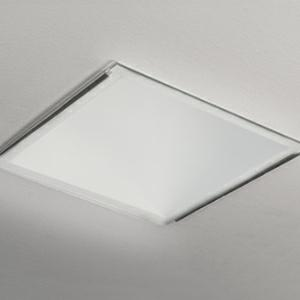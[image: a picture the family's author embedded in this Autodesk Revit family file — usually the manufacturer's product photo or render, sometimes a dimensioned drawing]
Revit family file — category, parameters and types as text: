
# Revit family: 3f_filippi_-_lucequadro_vs_3f_filippi_-_36575_-_lucequadro_led_2000_vs
name_source: partatom
category: Lighting Fixtures
units: mm (PartAtom-declared; Revit-internal decimal feet)

## family parameters
Cut with Voids When Loaded = No
Host = Face
Light Source = No
Part Type = Normal
Room Calculation Point = No
Round Connector Dimension = Use Diameter
Shared = No

## types (1)
- 3F Filippi - Lucequadro VS (1 x LED, 2291 lm, 20 W, 4000 K)
    Apparent Load = 20 VA
    Approval mark = ENEC
    CIE Flux Codes = 79 96 99 100 100
    Color Rendering = 80
    Color Temperature = 4000 K
    Control Gear = Electronic ballast
    Default Elevation = 1800 mm
    Description = ILLUMINOTECHNICAL
Luminous efficiency 100% (DLOR 100%, ULOR 0%).
Initial luminous flux of the luminaire 2291 lm.
Direct symmetric distribution.
Installation Interdistance Transv.D = 0.83 x hu - Long.D = 0.80 x hu.
Average luminance <3000 cd/m² for radial angles >65°.
Tabular UGR (CIE 117 - 4H-8H; S=0.25H; 70/50/20): RUG 17.2 - 17.
Beam angle: 58° - 57°.
Luminous efficacy 115 lm/W.
Lifetime (L90/B10): 30000 h. (tq+25°C)
Lifetime (L85/B10): 50000 h. (tq+25°C)
Lifetime (L70/B10): 80000 h. (tq+25°C)
Sudden decreased luminous flux after 50000 hours: 0% (C0).
Photobiological safety in compliance with IEC/TR 62778: RG1 low risk, (IEC 62471).
In compliance with IEC/EN 62722-2-1 - IEC/EN 62717 standards.

SOURCE
Compact LED module 2000/840.
Energy efficiency class (UE 2019/2020 - UE 2019/2015): D.
CIE 13.3 Colour rendering index: CRI >80 (R9 <50%).
IES TM-30 Fidelity Index: Rf = 84 Rg = 95.
CCT nominal colour temperature 4000 K.
Colour initial tolerance (MacAdam): SDCM 3.
Zhaga Book 3 compliant.

MECHANICAL
Housing in white painted steel.
Passive heat dissipator in anodised aluminium, oversized, for optimum thermal management of the LED module.
Flow recuperator in specular aluminium with superficial titanium-magnesium treatment, non-iridescent.
Moulded tempered anti-glare non-combustible glass, thickness 4 mm.
Lock-in mounting of the glass in the lateral seats in specular aluminium.
Fixing brackets in galvanised steel.
Slot-cover polycarbonate casings.
Dimensions: 235x235 mm, height 116 mm. Weight 2.11 kg.
IP44 protection degree for exposed part, IP20 for recessed part.
Mechanical strength to impacts IK08 (5 joule).
Glow-wire test resistance 960°C.

ELECTRICAL
Wiring on a separate unit.
Halogen Free electronic wiring 230V-50/60Hz, power factor 0.95, THD <25%, constant output current, SELV, class II, 1 driver.
Power of the luminaire 20 W.
CE - IEC 60598-1 - EN 60598-1.
SAFE FLICKER: PstLM=<1 and SVM=<0.4 (IEC TR 61547-1 and IEC TR 63158), to ensure a more comfortable and safe light.
Ambient temperature from 0°C to +25°C.
Temperature class T6 max 85°C.
Relative humidity UR: <85%.

INSTALLATION
Pull-up recessed fitting.
False ceiling carving: 210x210 mm.
All accessories dedicated to this product are available on the Catalog and on our website www.3F-Filippi.com.

ACCESSORIES
A0189 - Pair of reinforcing brackets for mineral fibre, metal and plasterboard panels, height 20 mm.

APPLICATIONS
Transit areas, corridors, commercial environments, display areas, shops and shop windows.

WARNING
Luminaire designed for disposal/recycling at end-of-life.
Replaceable (LED only) light source by a professional. Replaceable control gear by a professional.
    Height = 0 mm  [stored 0 ft]
    Lamp = 1 x LED
    Lamp Light Flux = 2291 lm
    Lamp Power = 20 W
    Lamp count = 1
    Length = 235 mm
    Lifetime = 50000 h
    Luminous efficacy = 115 lm/W
    Manufacturer = 3F Filippi
    ModVariant = No
    Model = 3F Filippi - 36575 - Lucequadro LED 2000 VS
    Mounting Place = Ceiling
    Mounting Type = Recessed
    Number of Poles = 1
    OnlyDefault = Yes
    Power Factor = 1
    Product Name = 3F Filippi - Lucequadro VS
    Product group = recessed luminaire
    ProductGroupID = 4
    Protection Class = Protection class II
    Protection Degree = IP 20
    RLX_Detail_Level = 1
    RLX_Emergency_Light_Flux = 0 lm
    RLX_Emergency_Type = 0
    RLX_Emergency_Type_DB = No
    RlxData = <blob elided: 57097 chars, md5=3c345c65>
    Socket = socket
    Standby Power = 0 W
    System Light Flux = 2291 lm
    System Power = 20 W
    Type Comments = Product without accessories
    Type Image = 3ffilippi_36575.jpg
    URL = http://relux.com
    VarID = ---
    Voltage = 0 V
    Weight = 0.00 kg
    Width = 235 mm

note: [stored X ft] marks values corroborated as IEEE doubles in the binary element streams (Revit-internal decimal feet)

## geometry (parser evidence)
native form markers: Blend x4, Sweep x11
no freeform markers — native parametric forms only
